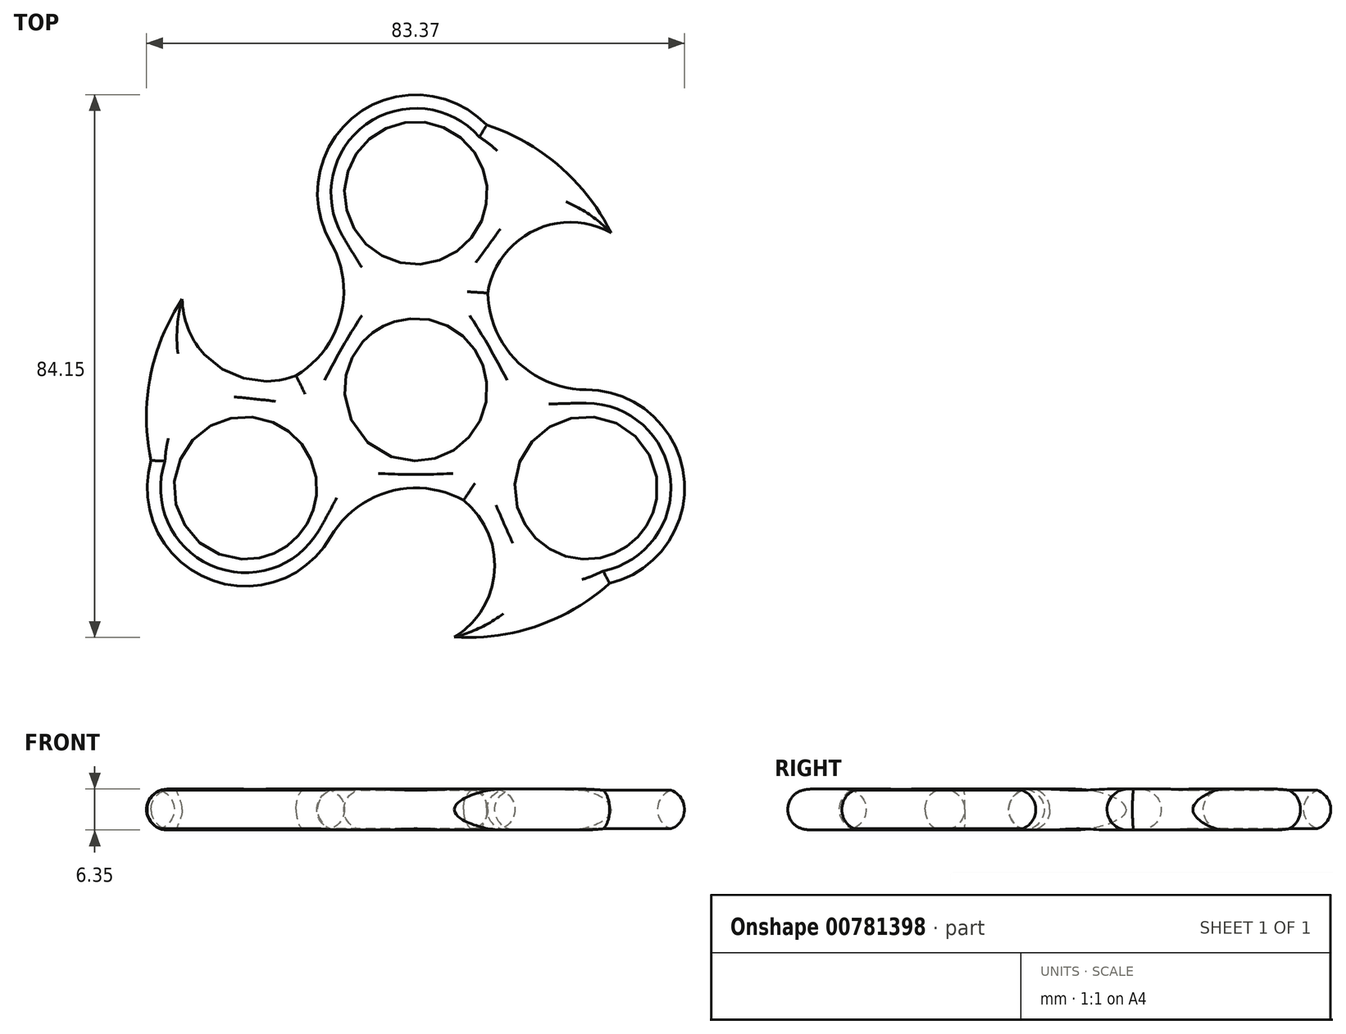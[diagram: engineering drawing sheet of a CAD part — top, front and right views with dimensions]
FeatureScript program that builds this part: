
annotation { "Feature Type Name" : "Feature", "Feature Type Description" : "" }
export const myFeature = defineFeature(function(context is Context, id is Id, definition is map)
    precondition{}
    {
        {
            var Q0;
            Q0=qCreatedBy(makeId("Top.planeOp"),FACE);
            var sketch = newSketch(context, id + "F0", { "sketchPlane" : qUnion([Q0])});
            skCircle(sketch, "E0", {"center": v(0, 0) * mm, "radius": 11.05 * mm});
            skCircle(sketch, "E1", {"center": v(0, 30.48) * mm, "radius": 11.05 * mm});
            skArc(sketch, "E2", {"start": v(11, 41.03) * mm, "mid": v(-9.15, 42.67) * mm, "end": v(-13.2, 22.86) * mm});
            skCircle(sketch, "E3.1.0", {"center": v(-26.4, -15.24) * mm, "radius": 11.05 * mm});
            skArc(sketch, "E3.1.1", {"start": v(-41.03, -10.99) * mm, "mid": v(-32.38, -29.26) * mm, "end": v(-13.2, -22.86) * mm});
            skCircle(sketch, "E3.2.0", {"center": v(26.4, -15.24) * mm, "radius": 11.05 * mm});
            skArc(sketch, "E3.2.1", {"start": v(30.03, -30.04) * mm, "mid": v(41.53, -13.41) * mm, "end": v(26.4, 0) * mm});
            skArc(sketch, "E4", {"start": v(-18.55, 2.17) * mm, "mid": v(-11.64, 11.42) * mm, "end": v(-13.2, 22.86) * mm});
            skArc(sketch, "E5.1.0", {"start": v(7.4, -17.15) * mm, "mid": v(-4.07, -15.8) * mm, "end": v(-13.2, -22.86) * mm});
            skArc(sketch, "E5.2.0", {"start": v(11.16, 14.98) * mm, "mid": v(15.71, 4.37) * mm, "end": v(26.4, 0) * mm});
            skArc(sketch, "E6", {"start": v(30.24, 24.34) * mm, "mid": v(22.3, 34.62) * mm, "end": v(11, 41.03) * mm});
            skArc(sketch, "E7", {"start": v(30.24, 24.34) * mm, "mid": v(18.26, 24.64) * mm, "end": v(11.16, 14.98) * mm});
            skArc(sketch, "E8.1.0", {"start": v(-36.2, 14.01) * mm, "mid": v(-41.14, 2) * mm, "end": v(-41.03, -10.99) * mm});
            skArc(sketch, "E8.1.1", {"start": v(-36.2, 14.01) * mm, "mid": v(-30.46, 3.5) * mm, "end": v(-18.55, 2.17) * mm});
            skArc(sketch, "E8.2.0", {"start": v(5.96, -38.36) * mm, "mid": v(18.84, -36.62) * mm, "end": v(30.03, -30.04) * mm});
            skArc(sketch, "E8.2.1", {"start": v(5.96, -38.36) * mm, "mid": v(12.2, -28.13) * mm, "end": v(7.4, -17.15) * mm});
            skPoint(sketch, "E9.orphan", {"position": v(13.2, 22.86) * mm});
            skPoint(sketch, "E10.orphan", {"position": v(13.2, -22.86) * mm});
            skPoint(sketch, "E11.orphan", {"position": v(-26.4, 0) * mm});
            skSolve(sketch);
        }
        {
            var Q0;
            Q0=qSketchRegion(id+"F0",true);
            extrude(context, id + "F1", {"entities" : qUnion([Q0]), "depth" : 6.35 * mm, "offsetDistance" : 25.4 * mm});
        }
        {
            var Q0;
            Q0=makeQuery(id+"F1.opExtrude","CAP_FACE",FACE,{"disambiguationData":[OSD([sQuery(id+"F0.wireOp",EDGE,"ict1kz9F-ZJu5-n0xv-7yNY-cyaO9Ddmu6TZ"),sQuery(id+"F0.wireOp",EDGE,"E1"),sQuery(id+"F0.wireOp",EDGE,"E2"),sQuery(id+"F0.wireOp",EDGE,"E3.1.0"),sQuery(id+"F0.wireOp",EDGE,"E3.1.1"),sQuery(id+"F0.wireOp",EDGE,"E3.2.0"),sQuery(id+"F0.wireOp",EDGE,"E3.2.1"),sQuery(id+"F0.wireOp",EDGE,"E4"),sQuery(id+"F0.wireOp",EDGE,"E5.1.0"),sQuery(id+"F0.wireOp",EDGE,"E5.2.0")])],"isStart":false});
            var Q1;
            Q1=makeQuery(id+"F1.opExtrude","CAP_FACE",FACE,{"disambiguationData":[OSD([sQuery(id+"F0.wireOp",EDGE,"ict1kz9F-ZJu5-n0xv-7yNY-cyaO9Ddmu6TZ"),sQuery(id+"F0.wireOp",EDGE,"E1"),sQuery(id+"F0.wireOp",EDGE,"E2"),sQuery(id+"F0.wireOp",EDGE,"E3.1.0"),sQuery(id+"F0.wireOp",EDGE,"E3.1.1"),sQuery(id+"F0.wireOp",EDGE,"E3.2.0"),sQuery(id+"F0.wireOp",EDGE,"E3.2.1"),sQuery(id+"F0.wireOp",EDGE,"E4"),sQuery(id+"F0.wireOp",EDGE,"E5.1.0"),sQuery(id+"F0.wireOp",EDGE,"E5.2.0")])],"isStart":true});
            fillet(context, id + "F2", {"entities" : qUnion([Q0, Q1]), "radius" : 3.17 * mm, "tangentPropagation" : true, "allowEdgeOverflow" : false});
        }
    });
